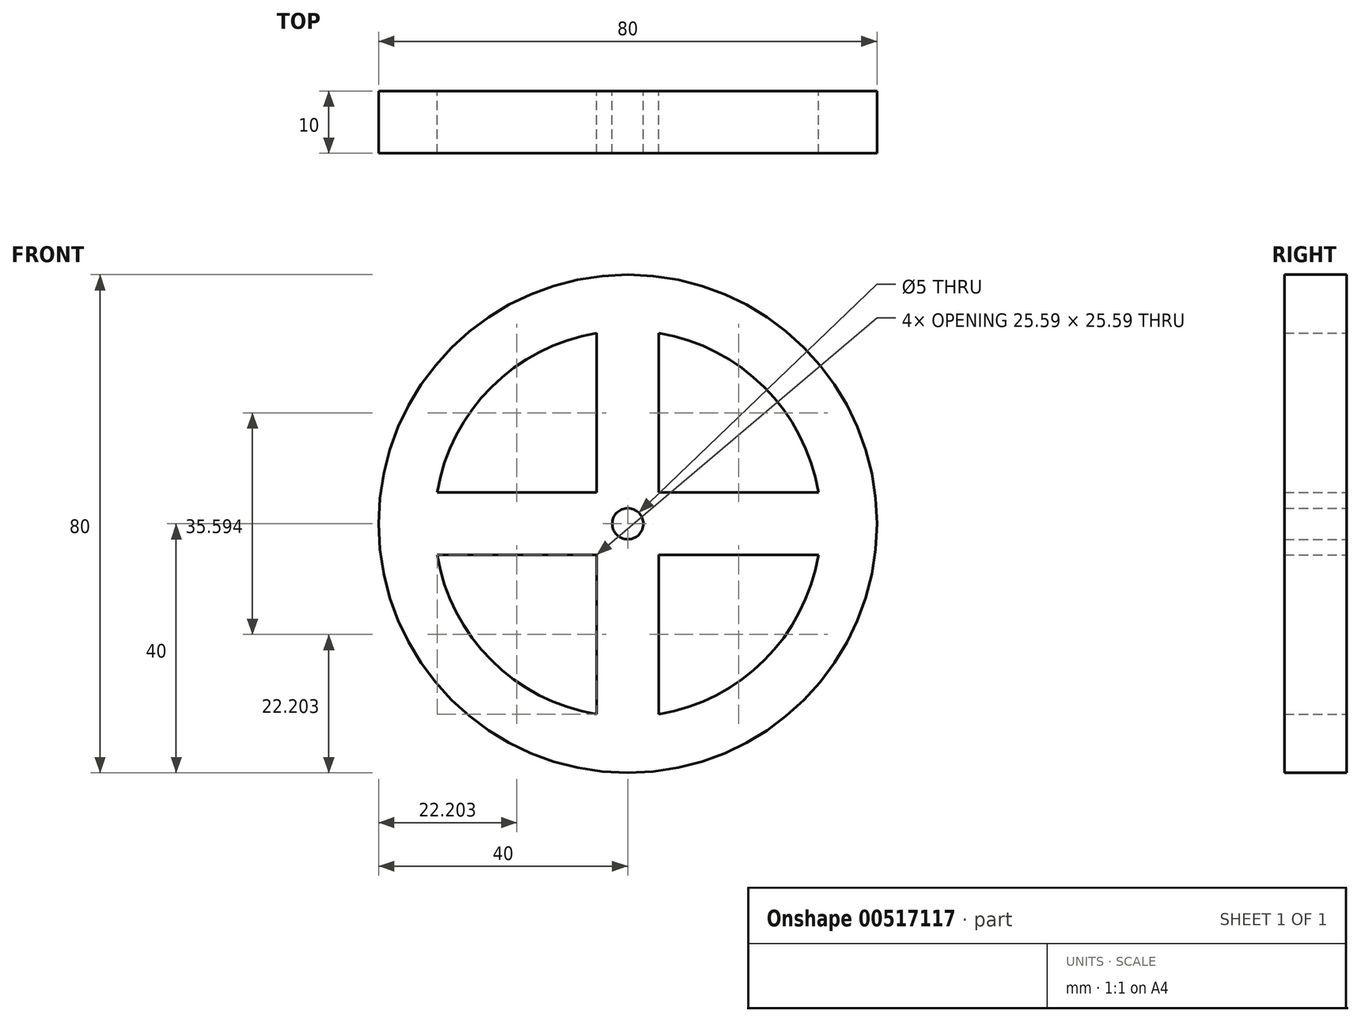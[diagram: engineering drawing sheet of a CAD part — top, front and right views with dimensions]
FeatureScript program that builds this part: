
annotation { "Feature Type Name" : "Feature", "Feature Type Description" : "" }
export const myFeature = defineFeature(function(context is Context, id is Id, definition is map)
    precondition{}
    {
        {
            var Q0;
            Q0=qCreatedBy(makeId("Front.planeOp"),FACE);
            var sketch = newSketch(context, id + "F0", { "sketchPlane" : qUnion([Q0])});
            skArc(sketch, "E0", {"start": v(-5, 30.6) * mm, "mid": v(-21.92, 21.92) * mm, "end": v(-30.6, 5) * mm});
            skCircle(sketch, "E1", {"center": v(0, 0) * mm, "radius": 2.5 * mm});
            skLineSegment(sketch, "E2", {"start": v(0, 0) * mm, "end": v(31, 0) * mm});
            skLineSegment(sketch, "E3", {"start": v(0, 0) * mm, "end": v(0, -31) * mm});
            skLineSegment(sketch, "E4", {"start": v(0, 0) * mm, "end": v(0, 2.5) * mm});
            skLineSegment(sketch, "E5", {"start": v(0, 0) * mm, "end": v(-31, 0) * mm});
            skLineSegment(sketch, "E6.0", {"start": v(-5, 5) * mm, "end": v(-5, 30.6) * mm});
            skLineSegment(sketch, "E7.0", {"start": v(5, 5) * mm, "end": v(5, 30.6) * mm});
            skLineSegment(sketch, "E8.0", {"start": v(-5, 5) * mm, "end": v(-30.6, 5) * mm});
            skLineSegment(sketch, "E9.0", {"start": v(-5, -5) * mm, "end": v(-30.6, -5) * mm});
            skLineSegment(sketch, "E10.0", {"start": v(5, -5) * mm, "end": v(5, -30.6) * mm});
            skLineSegment(sketch, "E11.0", {"start": v(-5, -5) * mm, "end": v(-5, -30.6) * mm});
            skLineSegment(sketch, "E12.0", {"start": v(5, -5) * mm, "end": v(30.6, -5) * mm});
            skLineSegment(sketch, "E13.0", {"start": v(5, 5) * mm, "end": v(30.6, 5) * mm});
            skCircle(sketch, "E14", {"center": v(0, 0) * mm, "radius": 40 * mm});
            skArc(sketch, "E15.trimOffspring", {"start": v(-30.6, -5) * mm, "mid": v(-21.92, -21.92) * mm, "end": v(-5, -30.6) * mm});
            skArc(sketch, "E16.trimOffspring", {"start": v(30.6, 5) * mm, "mid": v(21.92, 21.92) * mm, "end": v(5, 30.6) * mm});
            skArc(sketch, "E17.trimOffspring", {"start": v(5, -30.6) * mm, "mid": v(21.92, -21.92) * mm, "end": v(30.6, -5) * mm});
            skSolve(sketch);
        }
        {
            var Q0;
            Q0=makeQuery(id+"F0.imprint","IMPRINT",FACE,{"disambiguationData":[TD([[makeQuery(id+"F0.imprint","IMPRINT",EDGE,{"derivedFrom":sQuery(id+"F0.wireOp",EDGE,"E0")}),-1.0]])]});
            extrude(context, id + "F1", {"entities" : qUnion([Q0]), "depth" : 10 * mm, "offsetDistance" : 25 * mm});
        }
    });
